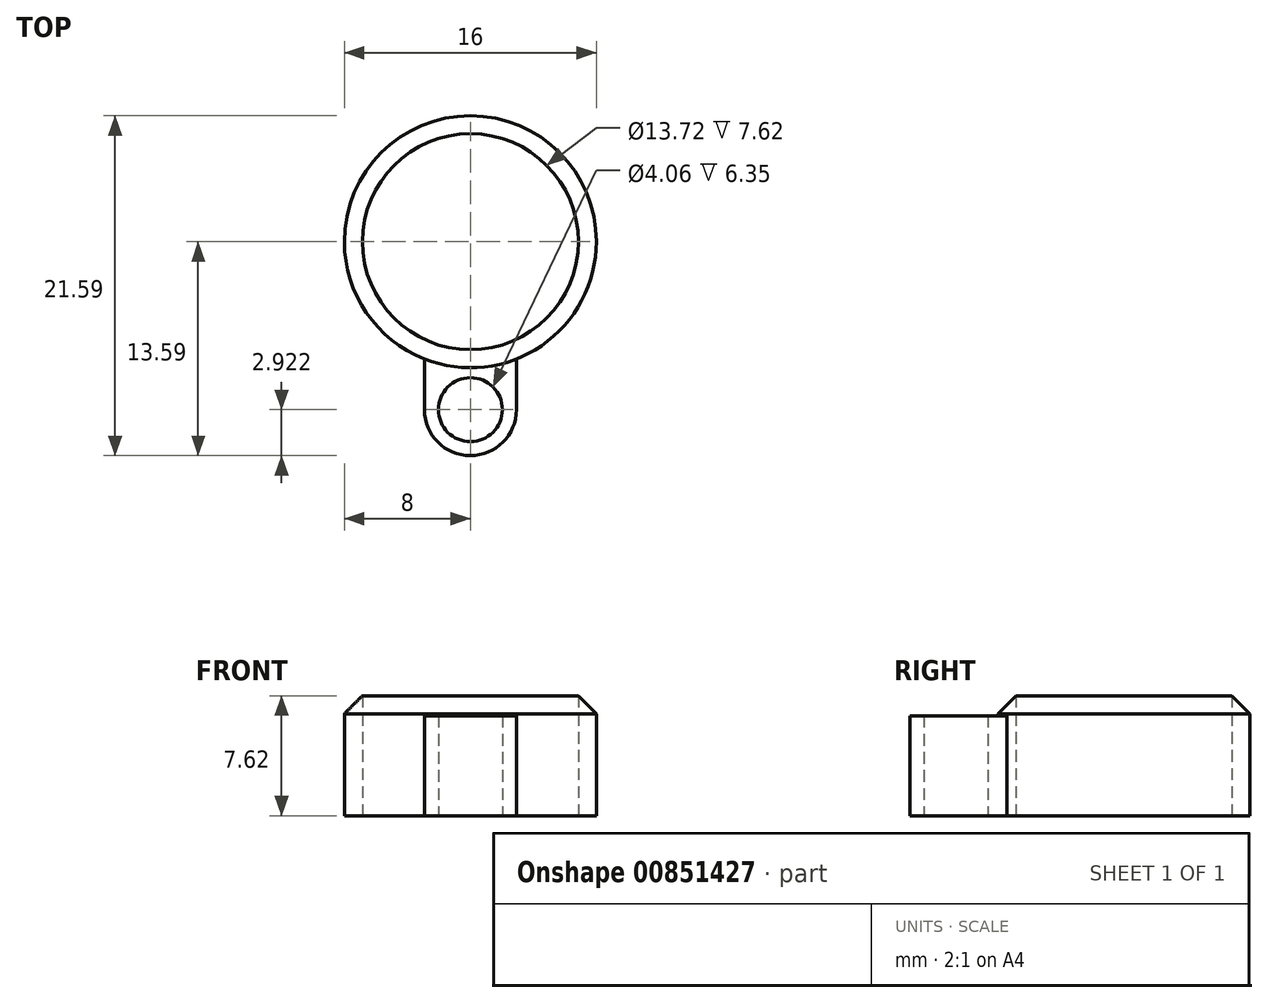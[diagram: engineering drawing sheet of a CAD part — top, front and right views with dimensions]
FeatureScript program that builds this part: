
annotation { "Feature Type Name" : "Feature", "Feature Type Description" : "" }
export const myFeature = defineFeature(function(context is Context, id is Id, definition is map)
    precondition{}
    {
        {
            var Q0;
            Q0=qCreatedBy(makeId("Top.planeOp"),FACE);
            var sketch = newSketch(context, id + "F0", { "sketchPlane" : qUnion([Q0])});
            skCircle(sketch, "E0", {"center": v(0, 0) * mm, "radius": 6.86 * mm});
            skCircle(sketch, "E1.0", {"center": v(0, 0) * mm, "radius": 8 * mm});
            skSolve(sketch);
        }
        {
            var Q0;
            Q0=makeQuery(id+"F0.imprint","IMPRINT",FACE,{"disambiguationData":[TD([[makeQuery(id+"F0.imprint","IMPRINT",EDGE,{"derivedFrom":sQuery(id+"F0.wireOp",EDGE,"E0")}),-1.0]])]});
            extrude(context, id + "F1", {"entities" : qUnion([Q0]), "depth" : 7.75 * mm, "offsetDistance" : 25.4 * mm});
        }
        {
            var Q0;
            Q0=makeQuery(id+"F1.opExtrude","CAP_EDGE",EDGE,{"disambiguationData":[OSD([sQuery(id+"F0.wireOp",EDGE,"E1.0")])],"isStart":false});
            chamfer(context, id + "F2", {"entities" : qUnion([Q0]), "chamferType" : ChamferType.TWO_OFFSETS, "width1" : 1.27 * mm, "oppositeDirection" : false, "width2" : 1.27 * mm, "tangentPropagation" : true});
        }
        {
            var Q0;
            Q0=makeQuery(id+"F1.opExtrude","CAP_FACE",FACE,{"disambiguationData":[OSD([sQuery(id+"F0.wireOp",EDGE,"E0"),sQuery(id+"F0.wireOp",EDGE,"E1.0")])],"isStart":true});
            var sketch = newSketch(context, id + "F3", { "sketchPlane" : qUnion([Q0])});
            skArc(sketch, "E2", {"start": v(2.92, 10.67) * mm, "mid": v(0, 13.59) * mm, "end": v(-2.92, 10.67) * mm});
            skLineSegment(sketch, "E3", {"start": v(2.92, 10.67) * mm, "end": v(2.92, 7.45) * mm});
            skLineSegment(sketch, "E4", {"start": v(-2.92, 10.67) * mm, "end": v(-2.92, 7.45) * mm});
            skLineSegment(sketch, "E5", {"start": v(-2.92, 7.45) * mm, "end": v(2.92, 7.45) * mm});
            skCircle(sketch, "E6", {"center": v(0, 10.67) * mm, "radius": 2.03 * mm});
            skSolve(sketch);
        }
        {
            var Q0;
            Q0=makeQuery(id+"F3.imprint","IMPRINT",FACE,{"disambiguationData":[TD([[makeQuery(id+"F3.imprint","IMPRINT",EDGE,{"derivedFrom":sQuery(id+"F3.wireOp",EDGE,"E2")}),1.0]])]});
            var Q1;
            Q1=makeQuery(id+"F2.opChamfer","BLEND_FACE",FACE,{"disambiguationData":[OSD([sQuery(id+"F0.wireOp",EDGE,"E1.0")])]});
            extrude(context, id + "F4", {"entities" : qUnion([Q0]), "operationType" : NewBodyOperationType.ADD, "oppositeDirection" : true, "depth" : 6.35 * mm, "endBoundEntityFace" : qUnion([Q1]), "offsetDistance" : 25.4 * mm});
        }
    });
